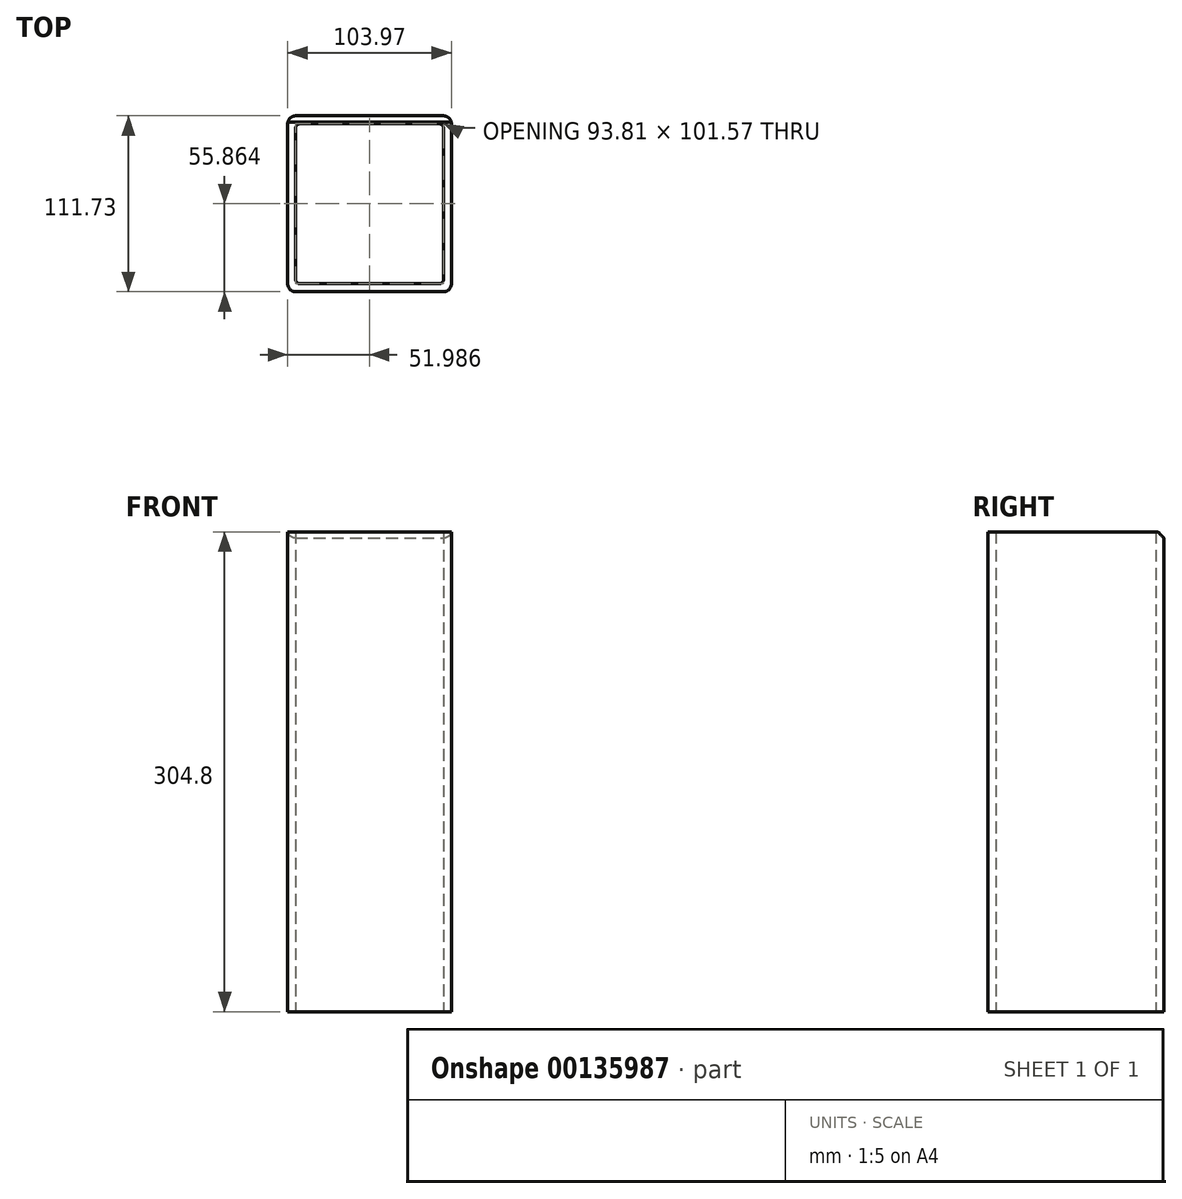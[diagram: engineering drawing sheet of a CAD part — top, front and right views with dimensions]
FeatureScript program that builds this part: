
annotation { "Feature Type Name" : "Feature", "Feature Type Description" : "" }
export const myFeature = defineFeature(function(context is Context, id is Id, definition is map)
    precondition{}
    {
        {
            assignVariable(context, id + "F0", {"name" : "Tube", "anyValue" : 4});
        }
        {
            var Q0;
            Q0=qCreatedBy(makeId("Top.planeOp"),FACE);
            var sketch = newSketch(context, id + "F1", { "sketchPlane" : qUnion([Q0])});
            skLineSegment(sketch, "E0.bottom", {"start": v(45.72, 50.8) * mm, "end": v(-48.09, 50.8) * mm});
            skLineSegment(sketch, "E0.top", {"start": v(45.72, -60.93) * mm, "end": v(-48.09, -60.93) * mm});
            skLineSegment(sketch, "E0.left", {"start": v(50.8, 45.72) * mm, "end": v(50.8, -55.85) * mm});
            skLineSegment(sketch, "E0.right", {"start": v(-53.17, 45.72) * mm, "end": v(-53.17, -55.85) * mm});
            skLineSegment(sketch, "E1.bottom", {"start": v(43.18, 45.72) * mm, "end": v(-45.55, 45.72) * mm});
            skLineSegment(sketch, "E1.top", {"start": v(43.18, -55.85) * mm, "end": v(-45.55, -55.85) * mm});
            skLineSegment(sketch, "E1.left", {"start": v(45.72, 43.18) * mm, "end": v(45.72, -53.31) * mm});
            skLineSegment(sketch, "E1.right", {"start": v(-48.09, 43.18) * mm, "end": v(-48.09, -53.31) * mm});
            skPoint(sketch, "E2.visualSharp", {"position": v(-48.09, 45.72) * mm});
            skArc(sketch, "E2.filletArc", {"start": v(-45.55, 45.72) * mm, "mid": v(-47.34, 44.98) * mm, "end": v(-48.09, 43.18) * mm});
            skPoint(sketch, "E3.visualSharp", {"position": v(-48.09, -55.85) * mm});
            skArc(sketch, "E3.filletArc", {"start": v(-48.09, -53.31) * mm, "mid": v(-47.34, -55.1) * mm, "end": v(-45.55, -55.85) * mm});
            skPoint(sketch, "E4.visualSharp", {"position": v(45.72, 45.72) * mm});
            skArc(sketch, "E4.filletArc", {"start": v(45.72, 43.18) * mm, "mid": v(44.98, 44.98) * mm, "end": v(43.18, 45.72) * mm});
            skPoint(sketch, "E5.visualSharp", {"position": v(45.72, -55.85) * mm});
            skArc(sketch, "E5.filletArc", {"start": v(43.18, -55.85) * mm, "mid": v(44.98, -55.1) * mm, "end": v(45.72, -53.31) * mm});
            skPoint(sketch, "E6.visualSharp", {"position": v(50.8, -60.93) * mm});
            skArc(sketch, "E6.filletArc", {"start": v(45.72, -60.93) * mm, "mid": v(49.31, -59.44) * mm, "end": v(50.8, -55.85) * mm});
            skPoint(sketch, "E7.visualSharp", {"position": v(-53.17, -60.93) * mm});
            skArc(sketch, "E7.filletArc", {"start": v(-53.17, -55.85) * mm, "mid": v(-51.68, -59.44) * mm, "end": v(-48.09, -60.93) * mm});
            skPoint(sketch, "E8.visualSharp", {"position": v(50.8, 50.8) * mm});
            skArc(sketch, "E8.filletArc", {"start": v(50.8, 45.72) * mm, "mid": v(49.31, 49.31) * mm, "end": v(45.72, 50.8) * mm});
            skPoint(sketch, "E9.visualSharp", {"position": v(-53.17, 50.8) * mm});
            skArc(sketch, "E9.filletArc", {"start": v(-48.09, 50.8) * mm, "mid": v(-51.68, 49.31) * mm, "end": v(-53.17, 45.72) * mm});
            skSolve(sketch);
        }
        {
            var Q0;
            Q0=makeQuery(id+"F1.imprint","IMPRINT",FACE,{"disambiguationData":[TD([[makeQuery(id+"F1.imprint","IMPRINT",EDGE,{"derivedFrom":sQuery(id+"F1.wireOp",EDGE,"E0.bottom")}),1.0]])]});
            extrude(context, id + "F2", {"entities" : qUnion([Q0]), "depth" : 304.8 * mm});
        }
        {
            var Q0;
            Q0=makeQuery(id+"F2.opExtrude","CAP_EDGE",EDGE,{"disambiguationData":[OSD([sQuery(id+"F1.wireOp",EDGE,"E0.bottom")])],"isStart":false});
            chamfer(context, id + "F3", {"entities" : qUnion([Q0]), "width" : (getVariable(context, 'Tube')) * mm});
        }
    });
